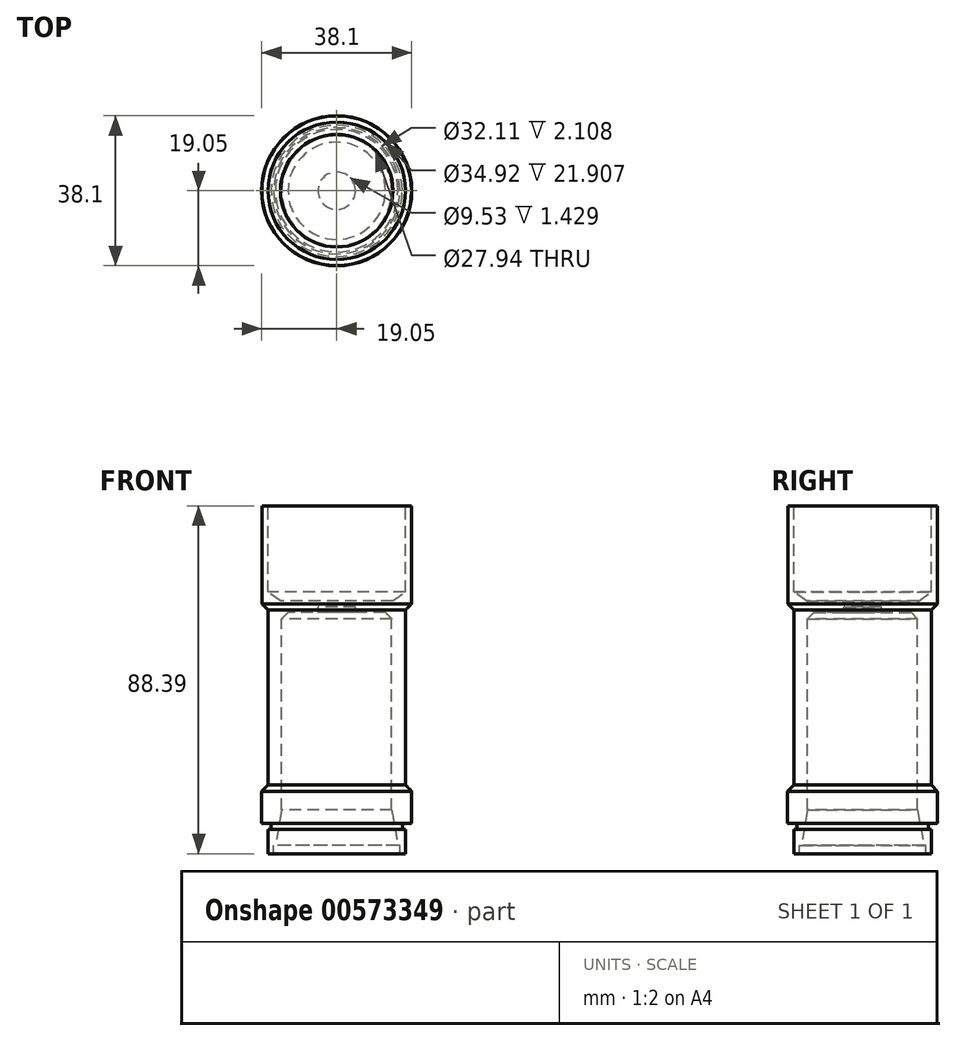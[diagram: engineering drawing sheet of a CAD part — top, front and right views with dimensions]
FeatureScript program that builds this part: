
annotation { "Feature Type Name" : "Feature", "Feature Type Description" : "" }
export const myFeature = defineFeature(function(context is Context, id is Id, definition is map)
    precondition{}
    {
        {
            var Q0;
            Q0=qCreatedBy(makeId("Front.planeOp"),FACE);
            var sketch = newSketch(context, id + "F0", { "sketchPlane" : qUnion([Q0])});
            skLineSegment(sketch, "E0", {"start": v(16.05, 0) * mm, "end": v(17.46, 0) * mm});
            skLineSegment(sketch, "E1", {"start": v(17.46, 0) * mm, "end": v(17.46, 6.16) * mm});
            skLineSegment(sketch, "E2", {"start": v(17.46, 6.16) * mm, "end": v(16.67, 6.16) * mm});
            skLineSegment(sketch, "E3", {"start": v(16.67, 6.16) * mm, "end": v(16.67, 7.75) * mm});
            skLineSegment(sketch, "E4", {"start": v(16.67, 7.75) * mm, "end": v(19.05, 7.75) * mm});
            skLineSegment(sketch, "E5", {"start": v(19.05, 7.75) * mm, "end": v(19.05, 15.88) * mm});
            skLineSegment(sketch, "E6", {"start": v(19.05, 15.88) * mm, "end": v(17.46, 17.46) * mm});
            skLineSegment(sketch, "E7", {"start": v(17.46, 17.46) * mm, "end": v(17.46, 61.91) * mm});
            skLineSegment(sketch, "E8", {"start": v(17.46, 61.91) * mm, "end": v(19.01, 63.46) * mm});
            skLineSegment(sketch, "E9", {"start": v(19.01, 63.46) * mm, "end": v(19.01, 88.4) * mm});
            skLineSegment(sketch, "E10", {"start": v(19.01, 88.4) * mm, "end": v(17.46, 88.4) * mm});
            skLineSegment(sketch, "E11", {"start": v(17.46, 88.4) * mm, "end": v(17.46, 66.49) * mm});
            skLineSegment(sketch, "E12", {"start": v(17.46, 66.49) * mm, "end": v(14.29, 64.26) * mm});
            skLineSegment(sketch, "E13", {"start": v(14.29, 64.26) * mm, "end": v(0, 64.26) * mm});
            skLineSegment(sketch, "E14", {"start": v(0, 64.26) * mm, "end": v(0, 62.74) * mm});
            skLineSegment(sketch, "E15", {"start": v(0, 62.74) * mm, "end": v(4.76, 62.74) * mm});
            skLineSegment(sketch, "E16", {"start": v(4.76, 62.74) * mm, "end": v(4.76, 61.3) * mm});
            skLineSegment(sketch, "E17", {"start": v(4.76, 61.3) * mm, "end": v(12.35, 61.3) * mm});
            skLineSegment(sketch, "E18", {"start": v(12.35, 61.3) * mm, "end": v(13.97, 59.7) * mm});
            skLineSegment(sketch, "E19", {"start": v(13.97, 59.7) * mm, "end": v(13.97, 11.11) * mm});
            skLineSegment(sketch, "E20", {"start": v(16.05, 0) * mm, "end": v(16.05, 2.1) * mm});
            skLineSegment(sketch, "E21", {"start": v(16.05, 2.1) * mm, "end": v(15.56, 2.1) * mm});
            skLineSegment(sketch, "E22", {"start": v(15.56, 2.1) * mm, "end": v(13.97, 11.11) * mm});
            skSolve(sketch);
        }
        {
            var Q0;
            Q0=makeQuery(id+"F0.imprint","IMPRINT",FACE,{"disambiguationData":[TD([[makeQuery(id+"F0.imprint","IMPRINT",EDGE,{"derivedFrom":sQuery(id+"F0.wireOp",EDGE,"E0")}),1.0]])]});
            var Q1;
            Q1=sQuery(id+"F0.wireOp",EDGE,"E14");
            revolve(context, id + "F1", {"entities" : qUnion([Q0]), "axis" : qUnion([Q1]), "revolveType" : RevolveType.FULL});
        }
    });
